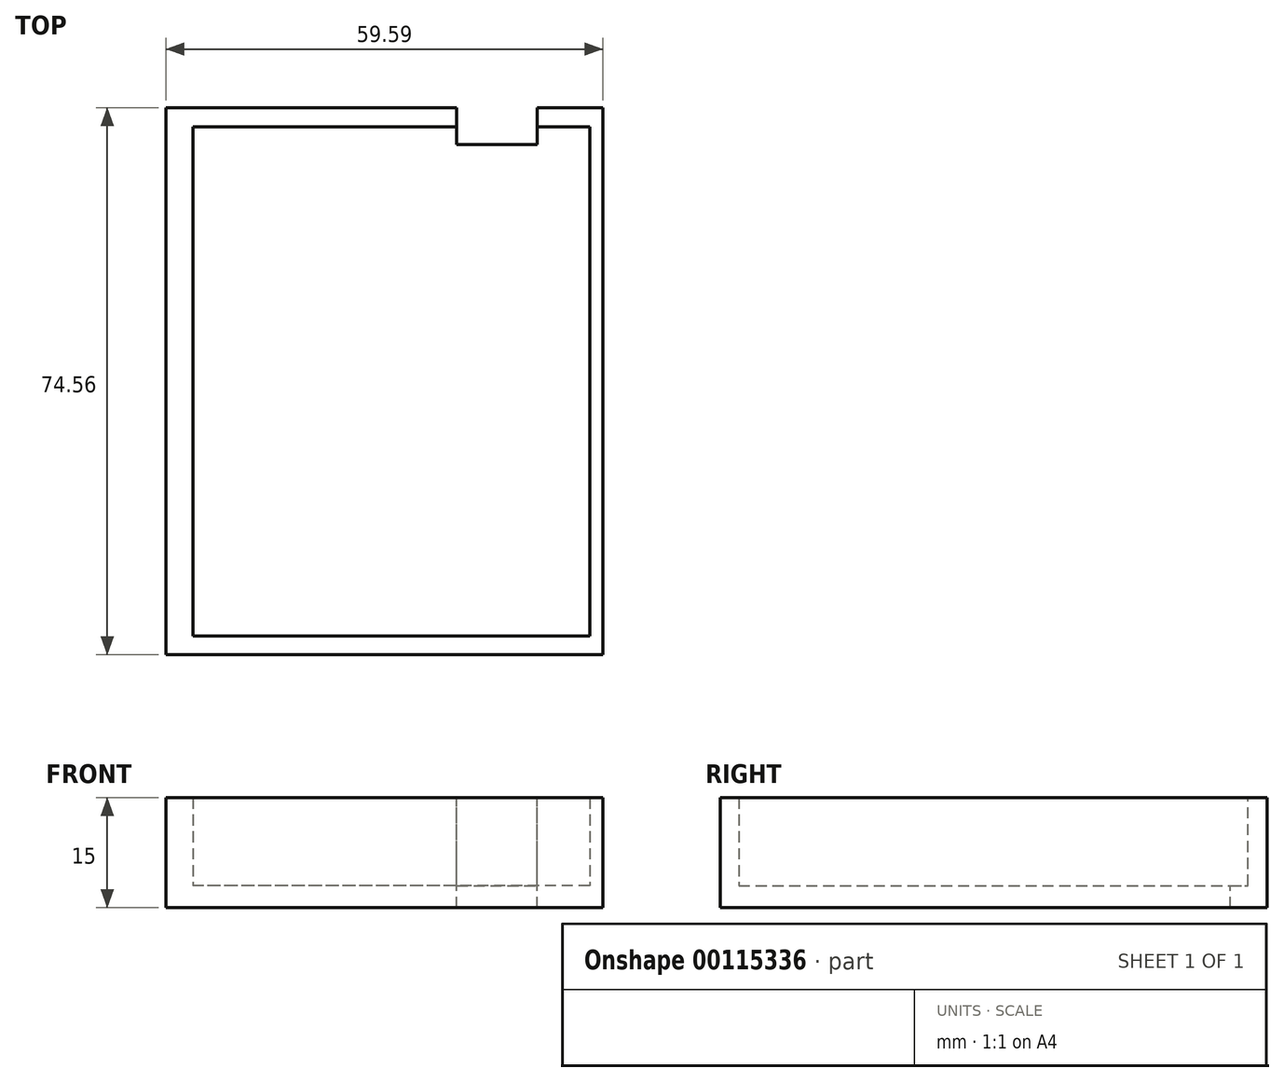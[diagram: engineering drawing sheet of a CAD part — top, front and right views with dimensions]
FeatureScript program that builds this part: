
annotation { "Feature Type Name" : "Feature", "Feature Type Description" : "" }
export const myFeature = defineFeature(function(context is Context, id is Id, definition is map)
    precondition{}
    {
        {
            var Q0;
            Q0=qCreatedBy(makeId("Top.planeOp"),FACE);
            var sketch = newSketch(context, id + "F0", { "sketchPlane" : qUnion([Q0])});
            skLineSegment(sketch, "E0.bottom", {"start": v(-18.65, 19.98) * mm, "end": v(35.45, 19.98) * mm});
            skLineSegment(sketch, "E0.top", {"start": v(-18.65, -49.47) * mm, "end": v(35.45, -49.47) * mm});
            skLineSegment(sketch, "E0.left", {"start": v(-18.65, 19.98) * mm, "end": v(-18.65, -49.47) * mm});
            skLineSegment(sketch, "E0.right", {"start": v(35.45, 19.98) * mm, "end": v(35.45, -49.47) * mm});
            skLineSegment(sketch, "E1.bottom", {"start": v(-22.31, 22.58) * mm, "end": v(37.28, 22.58) * mm});
            skLineSegment(sketch, "E1.top", {"start": v(-22.31, -51.98) * mm, "end": v(37.28, -51.98) * mm});
            skLineSegment(sketch, "E1.left", {"start": v(-22.31, 22.58) * mm, "end": v(-22.31, -51.98) * mm});
            skLineSegment(sketch, "E1.right", {"start": v(37.28, 22.58) * mm, "end": v(37.28, -51.98) * mm});
            skSolve(sketch);
        }
        {
            var Q0;
            Q0=makeQuery(id+"F0.imprint","IMPRINT",FACE,{"disambiguationData":[TD([[makeQuery(id+"F0.imprint","IMPRINT",EDGE,{"derivedFrom":sQuery(id+"F0.wireOp",EDGE,"E0.bottom")}),1.0]])]});
            extrude(context, id + "F1", {"entities" : qUnion([Q0]), "depth" : 15 * mm});
        }
        {
            var Q0;
            Q0=makeQuery(id+"F1.opExtrude","CAP_FACE",FACE,{"disambiguationData":[OSD([sQuery(id+"F0.wireOp",EDGE,"E0.bottom"),sQuery(id+"F0.wireOp",EDGE,"E0.top"),sQuery(id+"F0.wireOp",EDGE,"E0.left"),sQuery(id+"F0.wireOp",EDGE,"E0.right"),sQuery(id+"F0.wireOp",EDGE,"E1.bottom"),sQuery(id+"F0.wireOp",EDGE,"E1.top"),sQuery(id+"F0.wireOp",EDGE,"E1.left"),sQuery(id+"F0.wireOp",EDGE,"E1.right")])],"isStart":true});
            var sketch = newSketch(context, id + "F2", { "sketchPlane" : qUnion([Q0])});
            skLineSegment(sketch, "E2.bottom", {"start": v(-22.31, 51.98) * mm, "end": v(37.28, 51.98) * mm});
            skLineSegment(sketch, "E2.top", {"start": v(-22.31, -22.58) * mm, "end": v(37.28, -22.58) * mm});
            skLineSegment(sketch, "E2.left", {"start": v(-22.31, 51.98) * mm, "end": v(-22.31, -22.58) * mm});
            skLineSegment(sketch, "E2.right", {"start": v(37.28, 51.98) * mm, "end": v(37.28, -22.58) * mm});
            skSolve(sketch);
        }
        {
            var Q0;
            Q0 = qSketchRegion(id + "F2", true);
            extrude(context, id + "F3", {"entities" : qUnion([Q0]), "operationType" : NewBodyOperationType.ADD, "oppositeDirection" : true, "depth" : 3 * mm});
        }
        {
            var Q0;
            Q0=makeQuery(id+"F1.opExtrude","SWEPT_FACE",FACE,{"disambiguationData":[OSD([sQuery(id+"F0.wireOp",EDGE,"E1.bottom")])]});
            var sketch = newSketch(context, id + "F4", { "sketchPlane" : qUnion([Q0])});
            skLineSegment(sketch, "E3", {"start": v(-37.28, 0) * mm, "end": v(-28.28, 0) * mm});
            skLineSegment(sketch, "E4", {"start": v(-28.28, 0) * mm, "end": v(-17.34, 0) * mm});
            skLineSegment(sketch, "E5", {"start": v(-28.28, 0) * mm, "end": v(-28.28, 15) * mm});
            skLineSegment(sketch, "E6", {"start": v(-17.34, 0) * mm, "end": v(-17.34, 15) * mm});
            skLineSegment(sketch, "E7", {"start": v(-17.34, 15) * mm, "end": v(-28.28, 15) * mm});
            skSolve(sketch);
        }
        {
            var Q0;
            Q0 = qSketchRegion(id + "F4", true);
            extrude(context, id + "F5", {"entities" : qUnion([Q0]), "operationType" : NewBodyOperationType.REMOVE, "oppositeDirection" : true, "depth" : 5.04 * mm});
        }
    });
